# Revit family: FP-Revit20-en-EB60DSX1-CoffeeMaker-0-9000xxxx-AU-NZ-UK-IE-SG-EU
name_source: partatom
category: Generic Models
units: mm (PartAtom-declared; Revit-internal decimal feet)

## family parameters
Always vertical = Yes
Can host rebar = No
Cut with Voids When Loaded = No
Part Type = Normal
Room Calculation Point = No
Round Connector Dimension = Use Diameter
Shared = No
Work Plane-Based = No

## types (1)
- EB60DSX1
    Cavity - minimum depth = 545 mm  [stored 1.78806 ft]
    Cavity - minimum height = 450 mm  [stored 1.47638 ft]
    Cavity - minimum width = 560 mm  [stored 1.83727 ft]
    Chassis - Depth = 460 mm  [stored 1.50919 ft]
    Chassis - Height = 445 mm  [stored 1.45997 ft]
    Chassis - width = 560 mm  [stored 1.83727 ft]
    Connector Note = 220-240 V, 50Hz, 10 A
    Default Elevation = 0 mm  [stored 0 ft]
    Description = Built-in Coffee Maker, 60cm
    Manufacturer = Fisher & Paykel Appliances
    Material - Chassis = Fisher & Paykel - Aluminium
    Material - Glass = Fisher & Paykel - Glass, Black
    Material - Trim = Fisher & Paykel - Stainless Steel
    Model = EB60DSX1
    Product - Overall depth = 480 mm  [stored 1.5748 ft]
    Product - Overall height = 458 mm
    Product - Overall width = 596 mm  [stored 1.95538 ft]
    Product - width = 596 mm  [stored 1.95538 ft]
    URL = www.fisherpaykel.com

note: [stored X ft] marks values corroborated as IEEE doubles in the binary element streams (Revit-internal decimal feet)

## geometry (parser evidence)
native form markers: Sweep x1
no freeform markers — native parametric forms only
